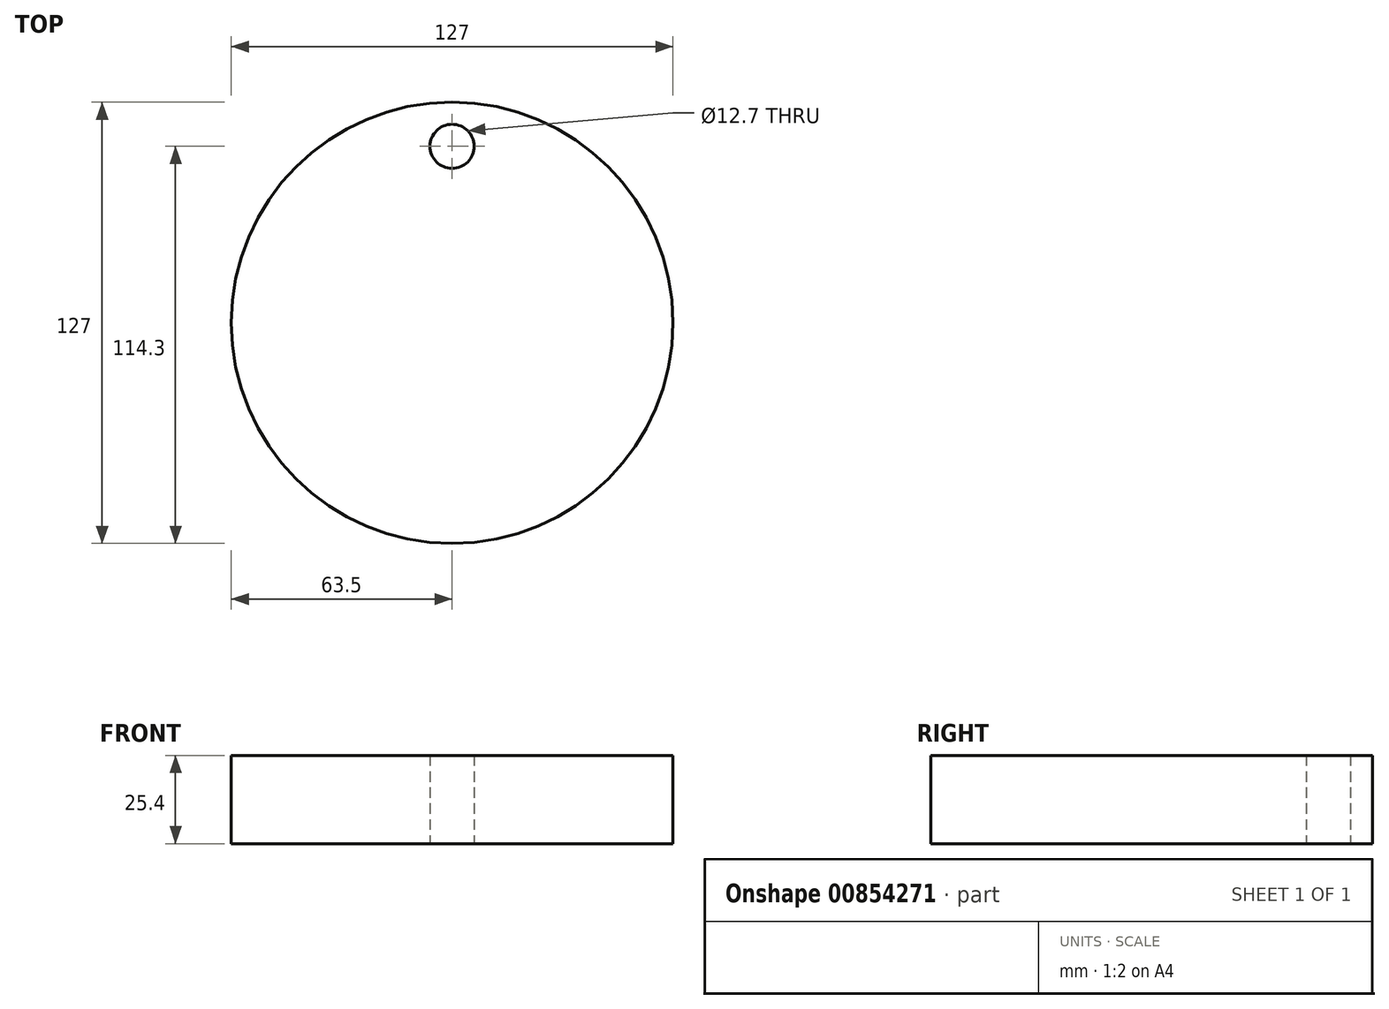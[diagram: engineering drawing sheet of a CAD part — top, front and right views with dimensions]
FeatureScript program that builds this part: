
annotation { "Feature Type Name" : "Feature", "Feature Type Description" : "" }
export const myFeature = defineFeature(function(context is Context, id is Id, definition is map)
    precondition{}
    {
        {
            var Q0;
            Q0=qCreatedBy(makeId("Top.planeOp"),FACE);
            var sketch = newSketch(context, id + "F0", { "sketchPlane" : qUnion([Q0])});
            skCircle(sketch, "E0", {"center": v(0, 0) * mm, "radius": 63.5 * mm});
            skSolve(sketch);
        }
        {
            var Q0;
            Q0 = qSketchRegion(id + "F0", true);
            extrude(context, id + "F1", {"entities" : qUnion([Q0]), "depth" : 25.4 * mm, "offsetDistance" : 25.4 * mm});
        }
        {
            var Q0;
            Q0=makeQuery(id+"F1.opExtrude","CAP_FACE",FACE,{"disambiguationData":[OSD([sQuery(id+"F0.wireOp",EDGE,"E0")])],"isStart":true});
            var sketch = newSketch(context, id + "F2", { "sketchPlane" : qUnion([Q0])});
            skPoint(sketch, "E1", {"position": v(0, -50.8) * mm});
            skSolve(sketch);
        }
        {
            var Q0;
            Q0=sQuery(id+"F2.wireOp",VERTEX,"E1");
            var Q1;
            Q1=makeQuery(id+"F1.opExtrude","SWEPT_BODY",BODY,{"disambiguationData":[OSD([sQuery(id+"F0.wireOp",EDGE,"E0")])]});
            hole(context, id + "F3", {"style" : HoleStyle.SIMPLE, "endStyle" : HoleEndStyle.THROUGH, "holeDiameter" : 12.7 * mm, "majorDiameter" : 6.35 * mm, "isTappedThrough" : true, "tappedDepth" : 12.7 * mm, "tapClearance" : 3, "locations" : qUnion([Q0]), "scope" : qUnion([Q1])});
        }
    });
